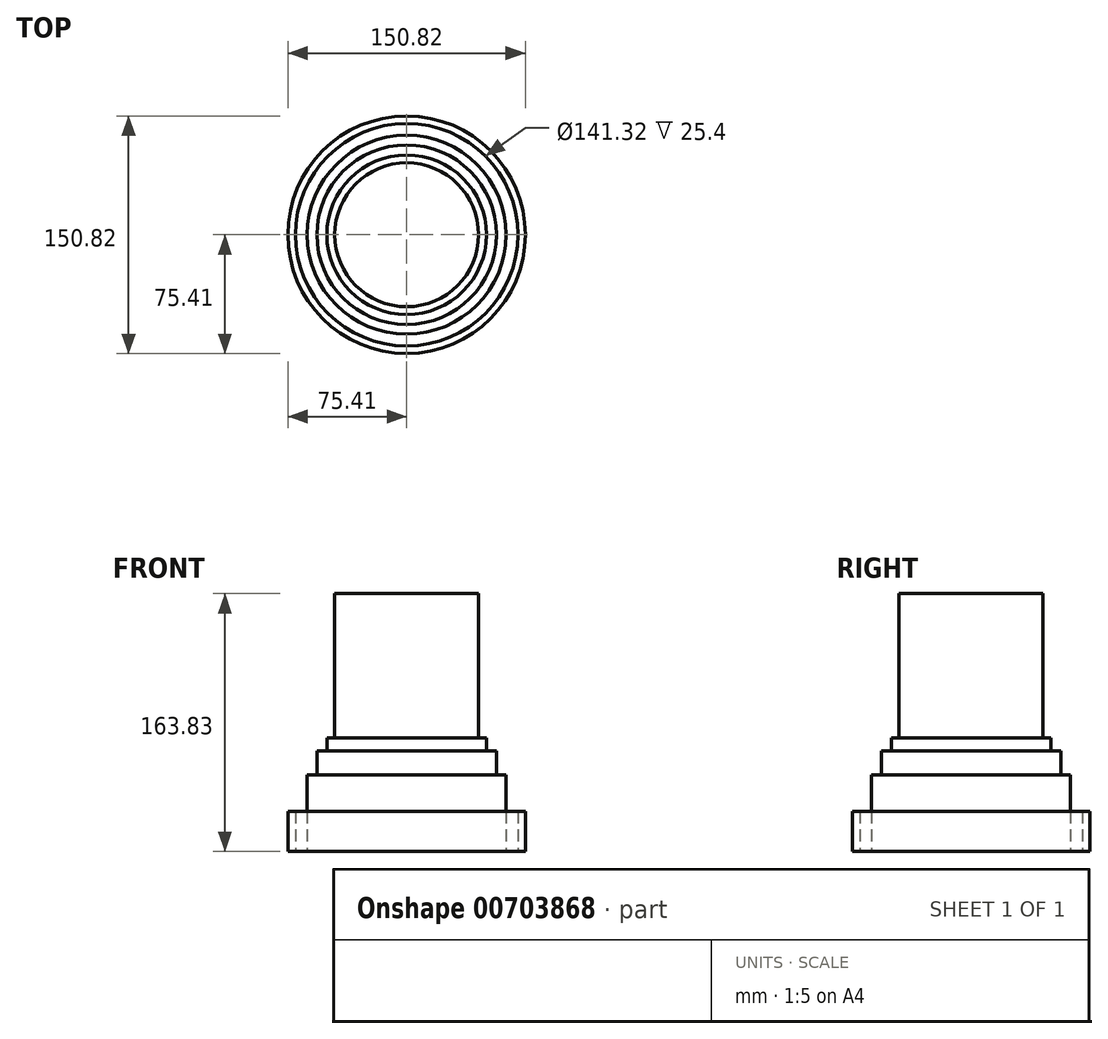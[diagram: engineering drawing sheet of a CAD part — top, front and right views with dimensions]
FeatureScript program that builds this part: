
annotation { "Feature Type Name" : "Feature", "Feature Type Description" : "" }
export const myFeature = defineFeature(function(context is Context, id is Id, definition is map)
    precondition{}
    {
        {
            var Q0;
            Q0=qCreatedBy(makeId("Top.planeOp"),FACE);
            var sketch = newSketch(context, id + "F0", { "sketchPlane" : qUnion([Q0])});
            skCircle(sketch, "E0", {"center": v(0, 0) * mm, "radius": 75.4 * mm});
            skCircle(sketch, "E1", {"center": v(0, 0) * mm, "radius": 70.66 * mm});
            skSolve(sketch);
        }
        {
            var Q0;
            Q0 = qSketchRegion(id + "F0", true);
            extrude(context, id + "F1", {"entities" : qUnion([Q0]), "depth" : 25.4 * mm, "offsetDistance" : 25.4 * mm});
        }
        {
            var Q0;
            Q0 = qSketchRegion(id + "F0", true);
            var Q1;
            Q1=makeQuery(id+"F1.opExtrude","CAP_FACE",FACE,{"disambiguationData":[OSD([sQuery(id+"F0.wireOp",EDGE,"E0"),sQuery(id+"F0.wireOp",EDGE,"E1")])],"isStart":true});
            extrude(context, id + "F2", {"entities" : qUnion([Q0, Q1]), "operationType" : NewBodyOperationType.ADD, "depth" : 25.4 * mm, "offsetDistance" : 25.4 * mm});
        }
        {
            var Q0;
            Q0=qCreatedBy(makeId("Top.planeOp"),FACE);
            var sketch = newSketch(context, id + "F3", { "sketchPlane" : qUnion([Q0])});
            skCircle(sketch, "E2", {"center": v(0, 0) * mm, "radius": 63.16 * mm});
            skSolve(sketch);
        }
        {
            var Q0;
            Q0 = qSketchRegion(id + "F3", true);
            extrude(context, id + "F4", {"entities" : qUnion([Q0]), "depth" : 48.5 * mm, "offsetDistance" : 25.4 * mm});
        }
        {
            var Q0;
            Q0=makeQuery(id+"F4.opExtrude","CAP_FACE",FACE,{"disambiguationData":[OSD([sQuery(id+"F3.wireOp",EDGE,"E2")])],"isStart":false});
            var sketch = newSketch(context, id + "F5", { "sketchPlane" : qUnion([Q0])});
            skCircle(sketch, "E3", {"center": v(0, 0) * mm, "radius": 57.02 * mm});
            skSolve(sketch);
        }
        {
            var Q0;
            Q0 = qSketchRegion(id + "F5", true);
            extrude(context, id + "F6", {"entities" : qUnion([Q0]), "operationType" : NewBodyOperationType.ADD, "depth" : 15.24 * mm, "offsetDistance" : 25.4 * mm});
        }
        {
            var Q0;
            Q0=makeQuery(id+"F6.opExtrude","CAP_FACE",FACE,{"disambiguationData":[OSD([sQuery(id+"F5.wireOp",EDGE,"E3")])],"isStart":false});
            var sketch = newSketch(context, id + "F7", { "sketchPlane" : qUnion([Q0])});
            skCircle(sketch, "E4", {"center": v(0, 0) * mm, "radius": 50.67 * mm});
            skSolve(sketch);
        }
        {
            var Q0;
            Q0 = qSketchRegion(id + "F7", true);
            extrude(context, id + "F8", {"entities" : qUnion([Q0]), "operationType" : NewBodyOperationType.ADD, "depth" : 8.38 * mm, "offsetDistance" : 25.4 * mm});
        }
        {
            var Q0;
            Q0=makeQuery(id+"F8.opExtrude","CAP_FACE",FACE,{"disambiguationData":[OSD([sQuery(id+"F7.wireOp",EDGE,"E4")])],"isStart":false});
            var sketch = newSketch(context, id + "F9", { "sketchPlane" : qUnion([Q0])});
            skCircle(sketch, "E5", {"center": v(0, 0) * mm, "radius": 45.71 * mm});
            skSolve(sketch);
        }
        {
            var Q0;
            Q0 = qSketchRegion(id + "F9", true);
            extrude(context, id + "F10", {"entities" : qUnion([Q0]), "operationType" : NewBodyOperationType.ADD, "depth" : 91.7 * mm, "offsetDistance" : 25.4 * mm});
        }
    });
